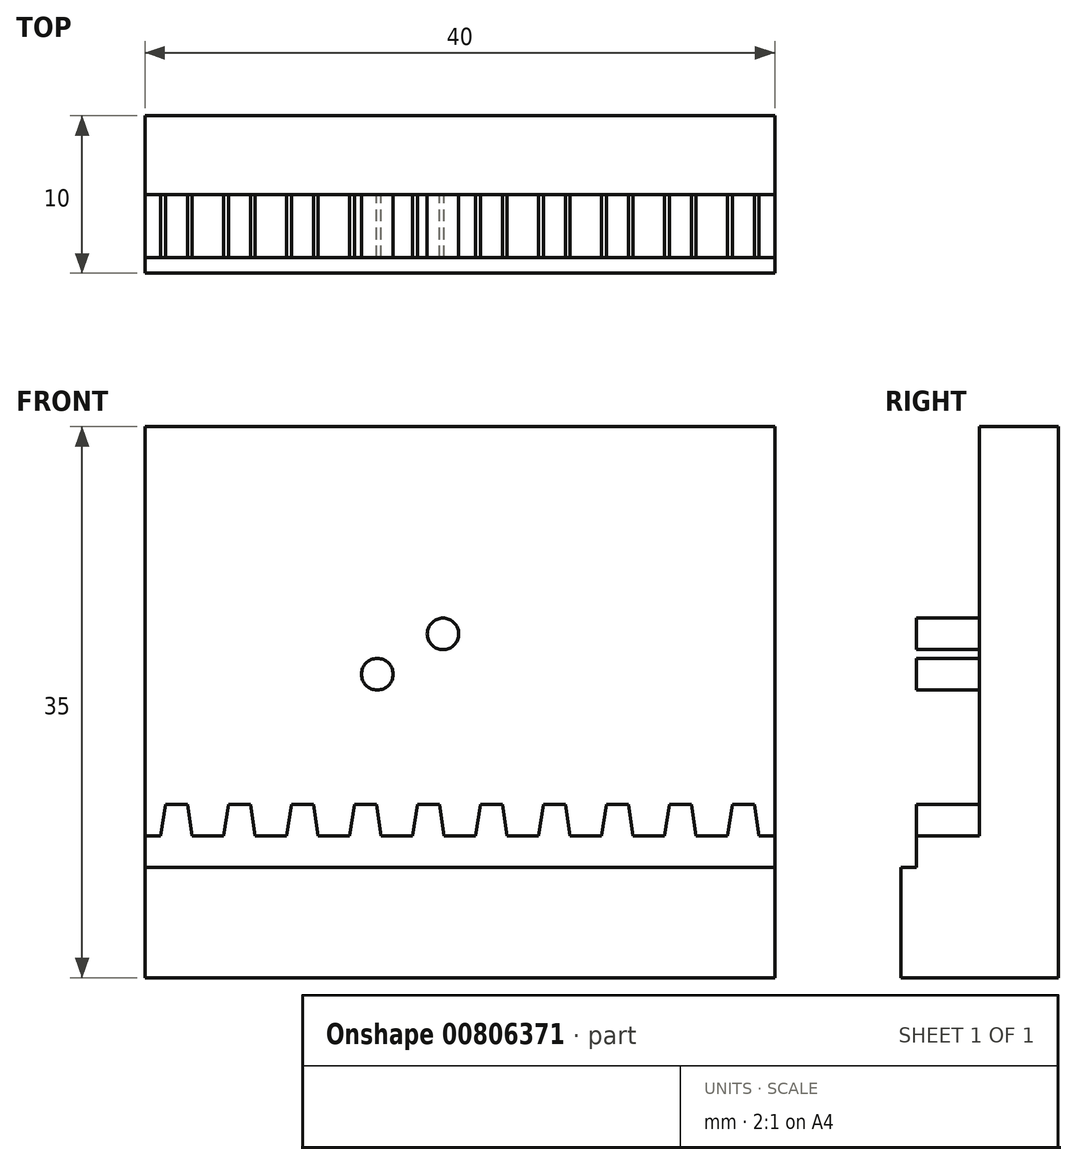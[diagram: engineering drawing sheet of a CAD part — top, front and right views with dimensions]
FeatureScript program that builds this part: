
annotation { "Feature Type Name" : "Feature", "Feature Type Description" : "" }
export const myFeature = defineFeature(function(context is Context, id is Id, definition is map)
    precondition{}
    {
        {
            var Q0;
            Q0=qCreatedBy(makeId("Front.planeOp"),FACE);
            var sketch = newSketch(context, id + "F0", { "sketchPlane" : qUnion([Q0])});
            skLineSegment(sketch, "E0.bottom", {"start": v(-20, 17.5) * mm, "end": v(20, 17.5) * mm});
            skLineSegment(sketch, "E0.top", {"start": v(-20, -17.5) * mm, "end": v(20, -17.5) * mm});
            skLineSegment(sketch, "E0.left", {"start": v(-20, 17.5) * mm, "end": v(-20, -17.5) * mm});
            skLineSegment(sketch, "E0.right", {"start": v(20, 17.5) * mm, "end": v(20, -17.5) * mm});
            skPoint(sketch, "E0.middle", {"position": v(0, 0) * mm});
            skSolve(sketch);
        }
        {
            var Q0;
            Q0=qSketchRegion(id+"F0",true);
            extrude(context, id + "F1", {"entities" : qUnion([Q0]), "depth" : 10 * mm, "offsetDistance" : 25 * mm});
        }
        {
            var Q0;
            Q0=makeQuery(id+"F1.opExtrude","CAP_FACE",FACE,{"disambiguationData":[OSD([sQuery(id+"F0.wireOp",EDGE,"E0.bottom"),sQuery(id+"F0.wireOp",EDGE,"E0.top"),sQuery(id+"F0.wireOp",EDGE,"E0.left"),sQuery(id+"F0.wireOp",EDGE,"E0.right")])],"isStart":false});
            var sketch = newSketch(context, id + "F2", { "sketchPlane" : qUnion([Q0])});
            skLineSegment(sketch, "E1.bottom", {"start": v(-20, 17.5) * mm, "end": v(20, 17.5) * mm});
            skLineSegment(sketch, "E1.top", {"start": v(-20, -12.5) * mm, "end": v(20, -12.5) * mm});
            skLineSegment(sketch, "E1.left", {"start": v(-20, 17.5) * mm, "end": v(-20, -12.5) * mm});
            skLineSegment(sketch, "E1.right", {"start": v(20, 17.5) * mm, "end": v(20, -12.5) * mm});
            skSolve(sketch);
        }
        {
            var Q0;
            Q0=qSketchRegion(id+"F2",true);
            extrude(context, id + "F3", {"entities" : qUnion([Q0]), "operationType" : NewBodyOperationType.REMOVE, "oppositeDirection" : true, "depth" : 5 * mm, "offsetDistance" : 25 * mm});
        }
        {
            var Q0;
            Q0=makeQuery(id+"F1.opExtrude","SWEPT_FACE",FACE,{"disambiguationData":[OSD([sQuery(id+"F0.wireOp",EDGE,"E0.right")])]});
            var sketch = newSketch(context, id + "F4", { "sketchPlane" : qUnion([Q0])});
            skLineSegment(sketch, "E2.bottom", {"start": v(-10, -12.5) * mm, "end": v(-9, -12.5) * mm});
            skLineSegment(sketch, "E2.top", {"start": v(-10, -10.5) * mm, "end": v(-9, -10.5) * mm});
            skLineSegment(sketch, "E2.left", {"start": v(-10, -12.5) * mm, "end": v(-10, -10.5) * mm});
            skLineSegment(sketch, "E2.right", {"start": v(-9, -12.5) * mm, "end": v(-9, -10.5) * mm});
            skSolve(sketch);
        }
        {
            var Q0;
            Q0=qSketchRegion(id+"F4",true);
            var Q1;
            Q1=makeQuery(id+"F1.opExtrude","SWEPT_FACE",FACE,{"disambiguationData":[OSD([sQuery(id+"F0.wireOp",EDGE,"E0.left")])]});
            extrude(context, id + "F5", {"entities" : qUnion([Q0]), "operationType" : NewBodyOperationType.ADD, "endBound" : BoundingType.UP_TO_SURFACE, "oppositeDirection" : true, "depth" : 25 * mm, "endBoundEntityFace" : qUnion([Q1]), "offsetDistance" : 25 * mm});
        }
        {
            var Q0;
            Q0=makeQuery(id+"F3.boolean.opBoolean","COPY",FACE,{"derivedFrom":makeQuery(id+"F3.opExtrude","CAP_FACE",FACE,{"disambiguationData":[OSD([sQuery(id+"F2.wireOp",EDGE,"E1.bottom"),sQuery(id+"F2.wireOp",EDGE,"E1.top"),sQuery(id+"F2.wireOp",EDGE,"E1.left"),sQuery(id+"F2.wireOp",EDGE,"E1.right")])],"isStart":false})});
            var sketch = newSketch(context, id + "F6", { "sketchPlane" : qUnion([Q0])});
            skCircle(sketch, "E3", {"center": v(-1.07, 4.34) * mm, "radius": 1 * mm});
            skCircle(sketch, "E4", {"center": v(-5.24, 1.78) * mm, "radius": 1 * mm});
            skSolve(sketch);
        }
        {
            var Q0;
            Q0=qSketchRegion(id+"F6",true);
            extrude(context, id + "F7", {"entities" : qUnion([Q0]), "operationType" : NewBodyOperationType.ADD, "depth" : 4 * mm, "offsetDistance" : 25 * mm});
        }
        {
            var Q0;
            Q0=makeQuery(id+"F3.boolean.opBoolean","COPY",FACE,{"derivedFrom":makeQuery(id+"F3.opExtrude","CAP_FACE",FACE,{"disambiguationData":[OSD([sQuery(id+"F2.wireOp",EDGE,"E1.bottom"),sQuery(id+"F2.wireOp",EDGE,"E1.top"),sQuery(id+"F2.wireOp",EDGE,"E1.left"),sQuery(id+"F2.wireOp",EDGE,"E1.right")])],"isStart":false})});
            var sketch = newSketch(context, id + "F8", { "sketchPlane" : qUnion([Q0])});
            skLineSegment(sketch, "E5.bottom", {"start": v(20, -12.5) * mm, "end": v(-20, -12.5) * mm});
            skLineSegment(sketch, "E5.top", {"start": v(20, -8.5) * mm, "end": v(-20, -8.5) * mm});
            skLineSegment(sketch, "E5.left", {"start": v(20, -12.5) * mm, "end": v(20, -8.5) * mm});
            skLineSegment(sketch, "E5.right", {"start": v(-20, -12.5) * mm, "end": v(-20, -8.5) * mm});
            skLineSegment(sketch, "E6", {"start": v(-18, -8.5) * mm, "end": v(-18, -12.5) * mm, "construction": true});
            skLineSegment(sketch, "E7", {"start": v(-19, -8.5) * mm, "end": v(-18.7, -6.5) * mm});
            skLineSegment(sketch, "E8", {"start": v(-18.7, -6.5) * mm, "end": v(-18, -6.5) * mm});
            skLineSegment(sketch, "E9.MirrorCS", {"start": v(-17, -8.5) * mm, "end": v(-17.3, -6.5) * mm});
            skLineSegment(sketch, "E10.MirrorCS", {"start": v(-17.3, -6.5) * mm, "end": v(-18, -6.5) * mm});
            skLineSegment(sketch, "E11.1.0.0", {"start": v(-15, -8.5) * mm, "end": v(-14.7, -6.5) * mm});
            skLineSegment(sketch, "E11.1.0.1", {"start": v(-14.7, -6.5) * mm, "end": v(-14, -6.5) * mm});
            skLineSegment(sketch, "E11.1.0.2", {"start": v(-13.3, -6.5) * mm, "end": v(-14, -6.5) * mm});
            skLineSegment(sketch, "E11.1.0.3", {"start": v(-13, -8.5) * mm, "end": v(-13.3, -6.5) * mm});
            skLineSegment(sketch, "E11.2.0.0", {"start": v(-11, -8.5) * mm, "end": v(-10.7, -6.5) * mm});
            skLineSegment(sketch, "E11.2.0.1", {"start": v(-10.7, -6.5) * mm, "end": v(-10, -6.5) * mm});
            skLineSegment(sketch, "E11.2.0.2", {"start": v(-9.3, -6.5) * mm, "end": v(-10, -6.5) * mm});
            skLineSegment(sketch, "E11.2.0.3", {"start": v(-9, -8.5) * mm, "end": v(-9.3, -6.5) * mm});
            skLineSegment(sketch, "E11.3.0.0", {"start": v(-7, -8.5) * mm, "end": v(-6.7, -6.5) * mm});
            skLineSegment(sketch, "E11.3.0.1", {"start": v(-6.7, -6.5) * mm, "end": v(-6, -6.5) * mm});
            skLineSegment(sketch, "E11.3.0.2", {"start": v(-5.3, -6.5) * mm, "end": v(-6, -6.5) * mm});
            skLineSegment(sketch, "E11.3.0.3", {"start": v(-5, -8.5) * mm, "end": v(-5.3, -6.5) * mm});
            skLineSegment(sketch, "E11.4.0.0", {"start": v(-3, -8.5) * mm, "end": v(-2.7, -6.5) * mm});
            skLineSegment(sketch, "E11.4.0.1", {"start": v(-2.7, -6.5) * mm, "end": v(-2, -6.5) * mm});
            skLineSegment(sketch, "E11.4.0.2", {"start": v(-1.3, -6.5) * mm, "end": v(-2, -6.5) * mm});
            skLineSegment(sketch, "E11.4.0.3", {"start": v(-1, -8.5) * mm, "end": v(-1.3, -6.5) * mm});
            skLineSegment(sketch, "E11.5.0.0", {"start": v(1, -8.5) * mm, "end": v(1.3, -6.5) * mm});
            skLineSegment(sketch, "E11.5.0.1", {"start": v(1.3, -6.5) * mm, "end": v(2, -6.5) * mm});
            skLineSegment(sketch, "E11.5.0.2", {"start": v(2.7, -6.5) * mm, "end": v(2, -6.5) * mm});
            skLineSegment(sketch, "E11.5.0.3", {"start": v(3, -8.5) * mm, "end": v(2.7, -6.5) * mm});
            skLineSegment(sketch, "E11.6.0.0", {"start": v(5, -8.5) * mm, "end": v(5.3, -6.5) * mm});
            skLineSegment(sketch, "E11.6.0.1", {"start": v(5.3, -6.5) * mm, "end": v(6, -6.5) * mm});
            skLineSegment(sketch, "E11.6.0.2", {"start": v(6.7, -6.5) * mm, "end": v(6, -6.5) * mm});
            skLineSegment(sketch, "E11.6.0.3", {"start": v(7, -8.5) * mm, "end": v(6.7, -6.5) * mm});
            skLineSegment(sketch, "E11.7.0.0", {"start": v(9, -8.5) * mm, "end": v(9.3, -6.5) * mm});
            skLineSegment(sketch, "E11.7.0.1", {"start": v(9.3, -6.5) * mm, "end": v(10, -6.5) * mm});
            skLineSegment(sketch, "E11.7.0.2", {"start": v(10.7, -6.5) * mm, "end": v(10, -6.5) * mm});
            skLineSegment(sketch, "E11.7.0.3", {"start": v(11, -8.5) * mm, "end": v(10.7, -6.5) * mm});
            skLineSegment(sketch, "E11.8.0.0", {"start": v(13, -8.5) * mm, "end": v(13.3, -6.5) * mm});
            skLineSegment(sketch, "E11.8.0.1", {"start": v(13.3, -6.5) * mm, "end": v(14, -6.5) * mm});
            skLineSegment(sketch, "E11.8.0.2", {"start": v(14.7, -6.5) * mm, "end": v(14, -6.5) * mm});
            skLineSegment(sketch, "E11.8.0.3", {"start": v(15, -8.5) * mm, "end": v(14.7, -6.5) * mm});
            skLineSegment(sketch, "E11.9.0.0", {"start": v(17, -8.5) * mm, "end": v(17.3, -6.5) * mm});
            skLineSegment(sketch, "E11.9.0.1", {"start": v(17.3, -6.5) * mm, "end": v(18, -6.5) * mm});
            skLineSegment(sketch, "E11.9.0.2", {"start": v(18.7, -6.5) * mm, "end": v(18, -6.5) * mm});
            skLineSegment(sketch, "E11.9.0.3", {"start": v(19, -8.5) * mm, "end": v(18.7, -6.5) * mm});
            skLineSegment(sketch, "E11.direction1", {"start": v(-19, -8.5) * mm, "end": v(-15, -8.5) * mm, "construction": true});
            skSolve(sketch);
        }
        {
            var Q0;
            Q0=qSketchRegion(id+"F8",true);
            extrude(context, id + "F9", {"entities" : qUnion([Q0]), "operationType" : NewBodyOperationType.ADD, "depth" : 4 * mm, "offsetDistance" : 25 * mm});
        }
    });
